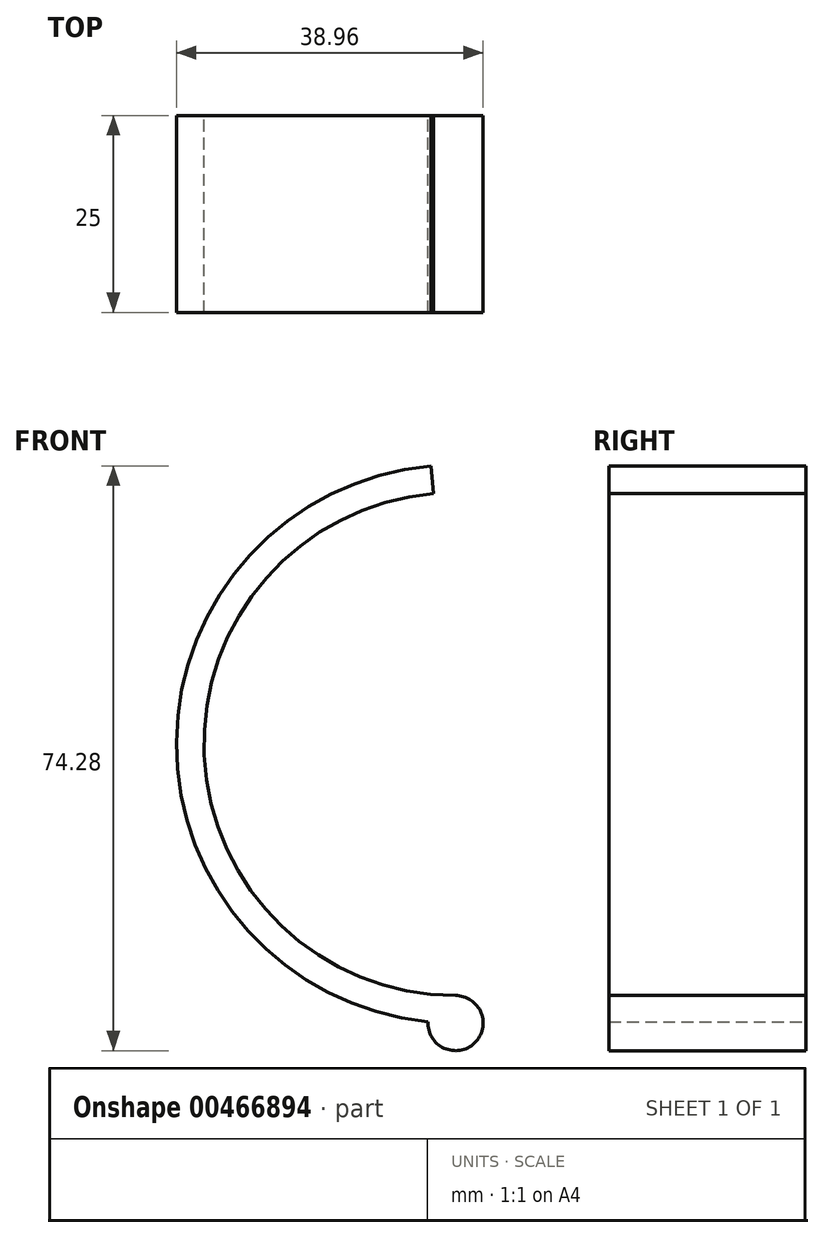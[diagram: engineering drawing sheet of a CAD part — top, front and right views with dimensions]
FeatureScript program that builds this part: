
annotation { "Feature Type Name" : "Feature", "Feature Type Description" : "" }
export const myFeature = defineFeature(function(context is Context, id is Id, definition is map)
    precondition{}
    {
        {
            var Q0;
            Q0=qCreatedBy(makeId("Front.planeOp"),FACE);
            var sketch = newSketch(context, id + "F0", { "sketchPlane" : qUnion([Q0])});
            skArc(sketch, "E0", {"start": v(-2.78, 63.8) * mm, "mid": v(-31.93, 30.56) * mm, "end": v(0, 0) * mm});
            skArc(sketch, "E1.0", {"start": v(-3.09, 67.28) * mm, "mid": v(-35.46, 32.16) * mm, "end": v(-3.5, -3.33) * mm});
            skLineSegment(sketch, "E2", {"start": v(-2.78, 63.8) * mm, "end": v(-3.09, 67.28) * mm});
            skArc(sketch, "E3", {"start": v(-3.5, -3.33) * mm, "mid": v(2.41, -6.04) * mm, "end": v(0, 0) * mm});
            skPoint(sketch, "E4.orphan", {"position": v(0, 63.91) * mm});
            skSolve(sketch);
        }
        {
            var Q0;
            Q0 = qSketchRegion(id + "F0", true);
            extrude(context, id + "F1", {"entities" : qUnion([Q0]), "depth" : 25 * mm});
        }
    });
